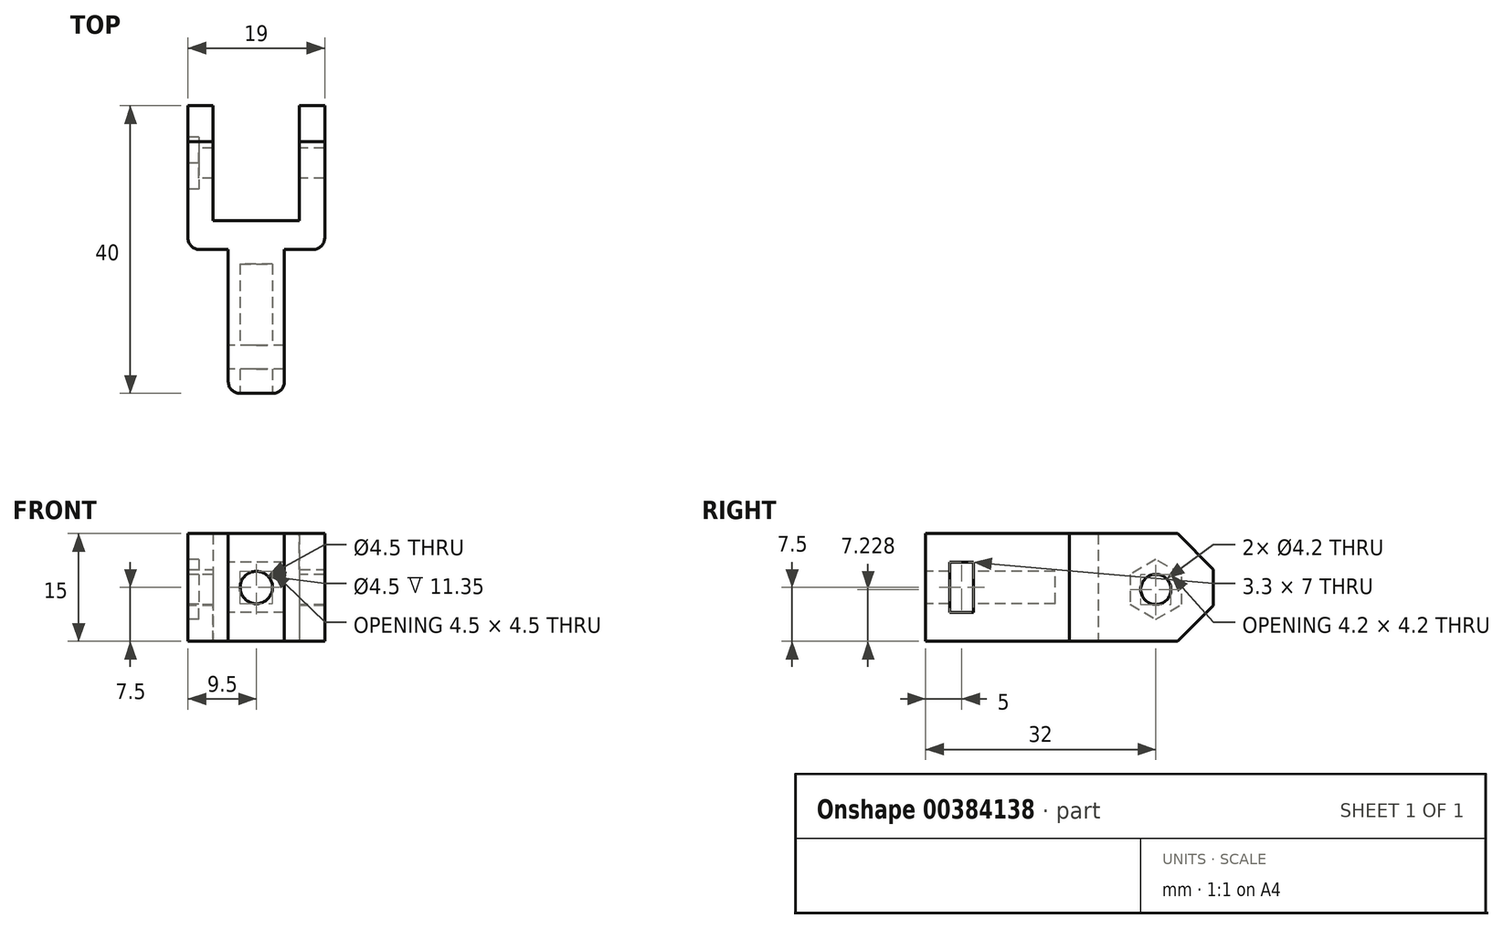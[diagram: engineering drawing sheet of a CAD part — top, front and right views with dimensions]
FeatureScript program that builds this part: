
annotation { "Feature Type Name" : "Feature", "Feature Type Description" : "" }
export const myFeature = defineFeature(function(context is Context, id is Id, definition is map)
    precondition{}
    {
        {
            var Q0;
            Q0=qCreatedBy(makeId("Top.planeOp"),FACE);
            var sketch = newSketch(context, id + "F0", { "sketchPlane" : qUnion([Q0])});
            skLineSegment(sketch, "E0", {"start": v(0, 0) * mm, "end": v(12, 0) * mm});
            skLineSegment(sketch, "E1", {"start": v(12, 0) * mm, "end": v(12, 16) * mm});
            skLineSegment(sketch, "E2", {"start": v(12, 16) * mm, "end": v(15.5, 16) * mm});
            skLineSegment(sketch, "E3", {"start": v(15.5, 16) * mm, "end": v(15.5, -4) * mm});
            skLineSegment(sketch, "E4", {"start": v(15.5, -4) * mm, "end": v(-3.5, -4) * mm});
            skLineSegment(sketch, "E5", {"start": v(-3.5, -4) * mm, "end": v(-3.5, 16) * mm});
            skLineSegment(sketch, "E6", {"start": v(-3.5, 16) * mm, "end": v(0, 16) * mm});
            skLineSegment(sketch, "E7", {"start": v(0, 16) * mm, "end": v(0, 0) * mm});
            skLineSegment(sketch, "E8", {"start": v(6, 0) * mm, "end": v(6, -31.45) * mm, "construction": true});
            skPoint(sketch, "E8.endSnap0", {"position": v(6, -4) * mm});
            skLineSegment(sketch, "E9", {"start": v(34.77, 16) * mm, "end": v(-22.08, 16) * mm, "construction": true});
            skLineSegment(sketch, "E10", {"start": v(6, -4) * mm, "end": v(2.1, -4) * mm});
            skLineSegment(sketch, "E11", {"start": v(2.1, -4) * mm, "end": v(2.1, -24) * mm});
            skLineSegment(sketch, "E12", {"start": v(2.1, -24) * mm, "end": v(9.9, -24) * mm});
            skLineSegment(sketch, "E13", {"start": v(9.9, -24) * mm, "end": v(9.9, -4) * mm});
            skSolve(sketch);
        }
        {
            var Q0;
            Q0 = qSketchRegion(id + "F0", true);
            extrude(context, id + "F1", {"entities" : qUnion([Q0]), "depth" : 15 * mm});
        }
        {
            var Q0;
            Q0=makeQuery(id+"F1.opExtrude","SWEPT_FACE",FACE,{"disambiguationData":[OSD([sQuery(id+"F0.wireOp",EDGE,"E12")])]});
            var sketch = newSketch(context, id + "F2", { "sketchPlane" : qUnion([Q0])});
            skLineSegment(sketch, "E14", {"start": v(2.1, 7.5) * mm, "end": v(9.9, 7.5) * mm, "construction": true});
            skLineSegment(sketch, "E15", {"start": v(6, 15) * mm, "end": v(6, 0) * mm, "construction": true});
            skCircle(sketch, "E16", {"center": v(6, 7.5) * mm, "radius": 2.25 * mm});
            skSolve(sketch);
        }
        {
            var Q0;
            Q0=makeQuery(id+"F2.imprint","IMPRINT",FACE,{"disambiguationData":[TD([[makeQuery(id+"F2.imprint","IMPRINT",EDGE,{"derivedFrom":sQuery(id+"F2.wireOp",EDGE,"E16")}),1.0]])]});
            extrude(context, id + "F3", {"entities" : qUnion([Q0]), "operationType" : NewBodyOperationType.REMOVE, "oppositeDirection" : true, "depth" : 18 * mm});
        }
        {
            var Q0;
            Q0=makeQuery(id+"F1.opExtrude","SWEPT_FACE",FACE,{"disambiguationData":[OSD([sQuery(id+"F0.wireOp",EDGE,"E5")])]});
            var sketch = newSketch(context, id + "F4", { "sketchPlane" : qUnion([Q0])});
            skLineSegment(sketch, "E17", {"start": v(0, 15.46) * mm, "end": v(0, -1) * mm, "construction": true});
            skLineSegment(sketch, "E18", {"start": v(0, 7.23) * mm, "end": v(-16, 7.23) * mm, "construction": true});
            skLineSegment(sketch, "E19", {"start": v(-8, 7.23) * mm, "end": v(-8, 15) * mm, "construction": true});
            skLineSegment(sketch, "E20", {"start": v(-8, 15) * mm, "end": v(-8, 0) * mm, "construction": true});
            skCircle(sketch, "E21", {"center": v(-8, 7.23) * mm, "radius": 2.1 * mm});
            skCircle(sketch, "E22.cCircle", {"center": v(-8, 7.23) * mm, "radius": 3.6 * mm, "construction": true});
            skLineSegment(sketch, "E22.0", {"start": v(-4.4, 9.3) * mm, "end": v(-4.4, 5.15) * mm});
            skLineSegment(sketch, "E22.1", {"start": v(-4.4, 5.15) * mm, "end": v(-8, 3.07) * mm});
            skLineSegment(sketch, "E22.2", {"start": v(-8, 3.07) * mm, "end": v(-11.6, 5.15) * mm});
            skLineSegment(sketch, "E22.3", {"start": v(-11.6, 5.15) * mm, "end": v(-11.6, 9.3) * mm});
            skLineSegment(sketch, "E22.4", {"start": v(-11.6, 9.3) * mm, "end": v(-8, 11.38) * mm});
            skLineSegment(sketch, "E22.5", {"start": v(-8, 11.38) * mm, "end": v(-4.4, 9.3) * mm});
            skPoint(sketch, "E22.0.midPoint", {"position": v(-4.4, 7.23) * mm});
            skSolve(sketch);
        }
        {
            var Q0;
            Q0=makeQuery(id+"F4.imprint","IMPRINT",FACE,{"disambiguationData":[TD([[makeQuery(id+"F4.imprint","IMPRINT",EDGE,{"derivedFrom":sQuery(id+"F4.wireOp",EDGE,"E21")}),1.0]])]});
            extrude(context, id + "F5", {"entities" : qUnion([Q0]), "operationType" : NewBodyOperationType.REMOVE, "oppositeDirection" : true, "depth" : 25 * mm});
        }
        {
            var Q0;
            Q0=makeQuery(id+"F1.opExtrude","SWEPT_FACE",FACE,{"disambiguationData":[OSD([sQuery(id+"F0.wireOp",EDGE,"E11")])]});
            var sketch = newSketch(context, id + "F6", { "sketchPlane" : qUnion([Q0])});
            skLineSegment(sketch, "E23", {"start": v(19, 15) * mm, "end": v(19, 0) * mm, "construction": true});
            skLineSegment(sketch, "E24", {"start": v(24, 7.5) * mm, "end": v(4, 7.5) * mm, "construction": true});
            skLineSegment(sketch, "E25.bottom", {"start": v(20.65, 11) * mm, "end": v(17.35, 11) * mm});
            skLineSegment(sketch, "E25.top", {"start": v(20.65, 4) * mm, "end": v(17.35, 4) * mm});
            skLineSegment(sketch, "E25.left", {"start": v(20.65, 11) * mm, "end": v(20.65, 4) * mm});
            skLineSegment(sketch, "E25.right", {"start": v(17.35, 11) * mm, "end": v(17.35, 4) * mm});
            skPoint(sketch, "E25.middle", {"position": v(19, 7.5) * mm});
            skSolve(sketch);
        }
        {
            var Q0;
            Q0=makeQuery(id+"F6.imprint","IMPRINT",FACE,{"disambiguationData":[TD([[makeQuery(id+"F6.imprint","IMPRINT",EDGE,{"derivedFrom":sQuery(id+"F6.wireOp",EDGE,"E25.bottom")}),1.0]])]});
            extrude(context, id + "F7", {"entities" : qUnion([Q0]), "operationType" : NewBodyOperationType.REMOVE, "oppositeDirection" : true, "depth" : 25 * mm});
        }
        {
            var Q0;
            Q0=makeQuery(id+"F1.opExtrude","SWEPT_EDGE",EDGE,{"disambiguationData":[OSD([sQuery(id+"F0.wireOp",EDGE,"E11"),sQuery(id+"F0.wireOp",EDGE,"E12")])]});
            var Q1;
            Q1=makeQuery(id+"F1.opExtrude","SWEPT_EDGE",EDGE,{"disambiguationData":[OSD([sQuery(id+"F0.wireOp",EDGE,"E12"),sQuery(id+"F0.wireOp",EDGE,"E13")])]});
            var Q2;
            Q2=makeQuery(id+"F1.opExtrude","SWEPT_EDGE",EDGE,{"disambiguationData":[OSD([sQuery(id+"F0.wireOp",EDGE,"E4"),sQuery(id+"F0.wireOp",EDGE,"E5")])]});
            var Q3;
            Q3=makeQuery(id+"F1.opExtrude","SWEPT_EDGE",EDGE,{"disambiguationData":[OSD([sQuery(id+"F0.wireOp",EDGE,"E3"),sQuery(id+"F0.wireOp",EDGE,"E4")])]});
            fillet(context, id + "F8", {"entities" : qUnion([Q0, Q1, Q2, Q3]), "radius" : 1.6 * mm, "tangentPropagation" : true, "allowEdgeOverflow" : false});
        }
        {
            var Q0;
            Q0=makeQuery(id+"F1.opExtrude","CAP_EDGE",EDGE,{"disambiguationData":[OSD([sQuery(id+"F0.wireOp",EDGE,"E6")])],"isStart":true});
            var Q1;
            Q1=makeQuery(id+"F1.opExtrude","CAP_EDGE",EDGE,{"disambiguationData":[OSD([sQuery(id+"F0.wireOp",EDGE,"E2")])],"isStart":true});
            var Q2;
            Q2=makeQuery(id+"F1.opExtrude","CAP_EDGE",EDGE,{"disambiguationData":[OSD([sQuery(id+"F0.wireOp",EDGE,"E2")])],"isStart":false});
            var Q3;
            Q3=makeQuery(id+"F1.opExtrude","CAP_EDGE",EDGE,{"disambiguationData":[OSD([sQuery(id+"F0.wireOp",EDGE,"E6")])],"isStart":false});
            chamfer(context, id + "F9", {"entities" : qUnion([Q0, Q1, Q2, Q3]), "width" : 5 * mm, "tangentPropagation" : true});
        }
        {
            var Q0;
            Q0=makeQuery(id+"F4.imprint","IMPRINT",FACE,{"disambiguationData":[TD([[makeQuery(id+"F4.imprint","IMPRINT",EDGE,{"derivedFrom":sQuery(id+"F4.wireOp",EDGE,"E21")}),-1.0]])]});
            extrude(context, id + "F10", {"entities" : qUnion([Q0]), "operationType" : NewBodyOperationType.REMOVE, "oppositeDirection" : true, "depth" : 1.5 * mm});
        }
    });
